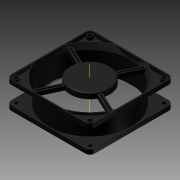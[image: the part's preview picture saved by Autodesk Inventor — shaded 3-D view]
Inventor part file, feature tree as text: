
AUTODESK INVENTOR PART (.ipt)
format: ipt  version: 2011 (Build 150239000, 239)  size: 355,840 bytes
history: native  units: mm (DEFAULTED — no unit token found)
features: sketch x11, extrude x7, fillet x3, plane x2, pattern_circular x2, revolve x1, hole x1, other x1, mirror x1
ambient origin geometry x8: Origin, YZ Plane, XZ Plane, XY Plane, X Axis, Y Axis, Z Axis, Center Point
bodies: Solid1 (feature_tree)
feature tree (29):
  revolve  "Revolution1"  [1 undecoded]
  plane  "Work Plane1"
  sketch  "Sketch2"  dims[d2=150.0deg d3=7.112mm]
  extrude  "Extrusion1"  Depth=7.112mm
  sketch  "Sketch3"  dims[d4=38.1mm d5=4.572mm d6=114.3mm d7=90.0deg]
  extrude  "Extrusion4"  Depth=4.572mm
  fillet  "Fillet2"  Radius=114.3mm
  fillet  "Fillet3"  [1 undecoded]
  extrude  "Extrusion5"  Depth=118.872mm
  extrude  "Extrusion6"  Depth=59.436mm
  hole  "Hole1"  [1 undecoded]
  other  "Work Axis1"
  pattern_circular  "Circular Pattern1"  [2 undecoded]
  mirror  "Mirror1"
  extrude  "Extrusion7"  Depth=5.08mm
  fillet  "Fillet4"  Radius=7.112mm
  sketch  "Sketch13"  dims[d17=1.016mm]
  plane  "Work Plane4"
  extrude  "Extrusion8"  Depth=0.762mm TaperAngle=0.0deg
  extrude  "Extrusion9"  Depth=7.62mm
  pattern_circular  "Circular Pattern2"  [2 undecoded]
  sketch  "Sketch1"  dims[d0=1.016mm d1=1.016mm]
  sketch  "Sketch6"  dims[d8=-19.05mm d9=118.872mm]
  sketch  "Sketch7"  dims[d10=118.872mm d11=59.436mm]
  sketch  "Sketch8"  dims[d12=59.436mm d13=25.4mm d14=0.0mm]
  sketch  "Sketch9"  dims[d15=1.016mm]
  sketch  "Sketch10"  dims[d16=1.016mm]
  sketch  "Sketch14"  dims[d18=1.016mm]
  sketch  "Sketch15"  dims[d27=1.778mm d28=6.096mm d29=0.0mm d30=5.08mm d31=7.112mm d32=0.762mm d33=0.0mm d34=7.62mm d35=4.7498mm d36=0.0mm d37=4.7498mm d38=12.7mm d39=9.525mm d40=6.35mm d41=14.3117mm d42=19.05mm d43=20.594885mm d44=40.0mm d46=360.0deg d47=55.88mm d48=7.62mm d49=0.0mm d50=1.524mm d51=5.588mm d52=3.048mm d53=5.588mm d54=3.048mm d55=0.0mm d56=3.048mm d57=0.0mm d58=40.0mm d60=360.0deg]
note: 7 required parameter values undecoded (feature->parameter linkage not recoverable at this tier; creation-order binding heuristic only, values carry confidence <= 0.55)